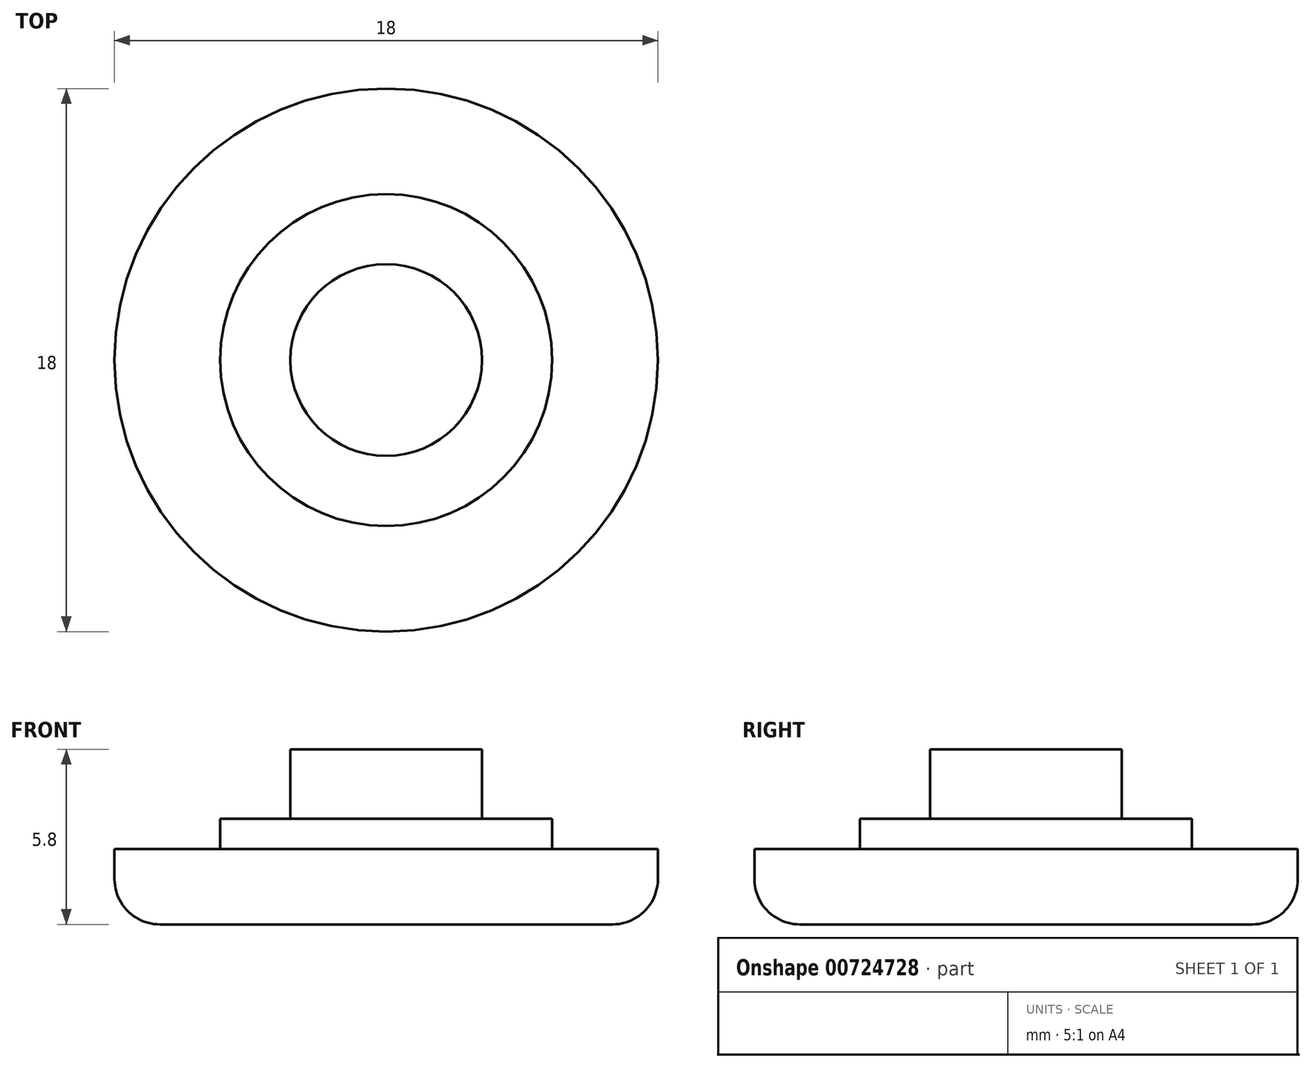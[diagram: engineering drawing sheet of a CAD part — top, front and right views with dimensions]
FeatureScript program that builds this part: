
annotation { "Feature Type Name" : "Feature", "Feature Type Description" : "" }
export const myFeature = defineFeature(function(context is Context, id is Id, definition is map)
    precondition{}
    {
        {
            var Q0;
            Q0=qCreatedBy(makeId("Top.planeOp"),FACE);
            var sketch = newSketch(context, id + "F0", { "sketchPlane" : qUnion([Q0])});
            skCircle(sketch, "E0", {"center": v(0, 0) * mm, "radius": 9 * mm});
            skCircle(sketch, "E1", {"center": v(0, 0) * mm, "radius": 3.17 * mm});
            skCircle(sketch, "E2", {"center": v(0, 0) * mm, "radius": 5.5 * mm});
            skSolve(sketch);
        }
        {
            var Q0;
            Q0=makeQuery(id+"F0.imprint","IMPRINT",FACE,{"disambiguationData":[TD([[makeQuery(id+"F0.imprint","IMPRINT",EDGE,{"derivedFrom":sQuery(id+"F0.wireOp",EDGE,"E0")}),1.0]])]});
            extrude(context, id + "F1", {"entities" : qUnion([Q0]), "depth" : 2.5 * mm, "offsetDistance" : 25 * mm});
        }
        {
            var Q0;
            Q0=makeQuery(id+"F0.imprint","IMPRINT",FACE,{"disambiguationData":[TD([[makeQuery(id+"F0.imprint","IMPRINT",EDGE,{"derivedFrom":sQuery(id+"F0.wireOp",EDGE,"E1")}),-1.0]])]});
            var Q1;
            Q1=makeQuery(id+"F1.opExtrude","CAP_FACE",FACE,{"disambiguationData":[OSD([sQuery(id+"F0.wireOp",EDGE,"E0"),sQuery(id+"F0.wireOp",EDGE,"E2")])],"isStart":false});
            extrude(context, id + "F2", {"entities" : qUnion([Q0]), "operationType" : NewBodyOperationType.ADD, "endBound" : BoundingType.UP_TO_SURFACE, "depth" : 25 * mm, "endBoundEntityFace" : qUnion([Q1]), "hasOffset" : true, "offsetDistance" : 1 * mm, "offsetOppositeDirection" : true});
        }
        {
            var Q0;
            Q0=makeQuery(id+"F0.imprint","IMPRINT",FACE,{"disambiguationData":[TD([[makeQuery(id+"F0.imprint","IMPRINT",EDGE,{"derivedFrom":sQuery(id+"F0.wireOp",EDGE,"E1")}),1.0]])]});
            var Q1;
            Q1=makeQuery(id+"F2.opExtrude","CAP_FACE",FACE,{"disambiguationData":[OSD([sQuery(id+"F0.wireOp",EDGE,"E0"),sQuery(id+"F0.wireOp",EDGE,"E2")])],"isStart":false});
            extrude(context, id + "F3", {"entities" : qUnion([Q0]), "operationType" : NewBodyOperationType.ADD, "endBound" : BoundingType.UP_TO_SURFACE, "depth" : 3 * mm, "endBoundEntityFace" : qUnion([Q1]), "hasOffset" : true, "offsetDistance" : 2.3 * mm, "offsetOppositeDirection" : true});
        }
        {
            var Q0;
            {var subQ0=sQuery(id+"F0.wireOp",EDGE,"E1");var subQ1=sQuery(id+"F0.wireOp",EDGE,"E2");Q0=makeQuery(id+"F3.boolean.opBoolean","MERGE",FACE,{"derivedFrom":[makeQuery(id+"F2.boolean.opBoolean","MERGE",FACE,{"derivedFrom":[makeQuery(id+"F1.opExtrude","CAP_FACE",FACE,{"disambiguationData":[OSD([sQuery(id+"F0.wireOp",EDGE,"E0"),subQ1])],"isStart":true}),makeQuery(id+"F2.opExtrude","CAP_FACE",FACE,{"disambiguationData":[OSD([subQ0,subQ1])],"isStart":true})]}),makeQuery(id+"F3.opExtrude","CAP_FACE",FACE,{"disambiguationData":[OSD([subQ0])],"isStart":true})]});}
            fillet(context, id + "F4", {"entities" : qUnion([Q0]), "radius" : 1.5 * mm, "tangentPropagation" : true, "allowEdgeOverflow" : false});
        }
    });
